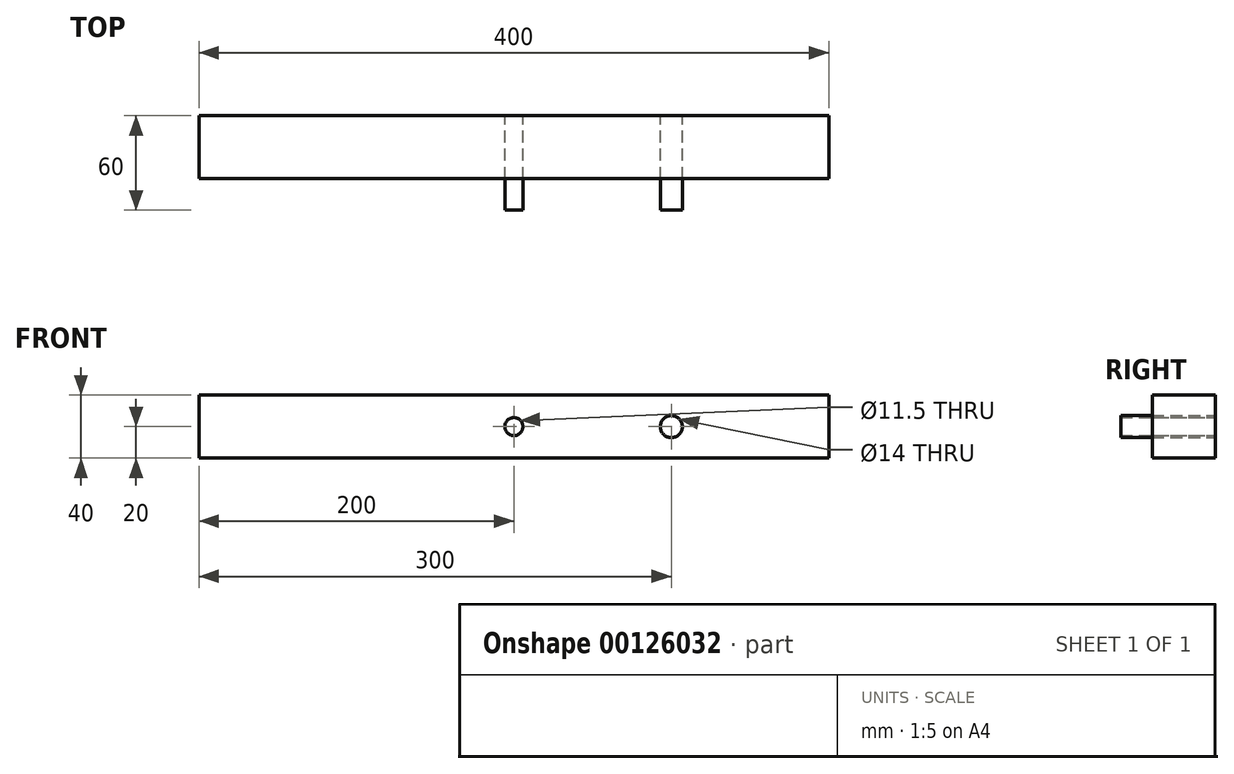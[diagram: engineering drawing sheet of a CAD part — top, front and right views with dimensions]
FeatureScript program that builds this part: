
annotation { "Feature Type Name" : "Feature", "Feature Type Description" : "" }
export const myFeature = defineFeature(function(context is Context, id is Id, definition is map)
    precondition{}
    {
        {
            var Q0;
            Q0=qCreatedBy(makeId("Front.planeOp"),FACE);
            var sketch = newSketch(context, id + "F0", { "sketchPlane" : qUnion([Q0])});
            skLineSegment(sketch, "E0.bottom", {"start": v(200, 20) * mm, "end": v(-200, 20) * mm});
            skLineSegment(sketch, "E0.top", {"start": v(200, -20) * mm, "end": v(-200, -20) * mm});
            skLineSegment(sketch, "E0.left", {"start": v(200, 20) * mm, "end": v(200, -20) * mm});
            skLineSegment(sketch, "E0.right", {"start": v(-200, 20) * mm, "end": v(-200, -20) * mm});
            skPoint(sketch, "E0.middle", {"position": v(0, 0) * mm});
            skCircle(sketch, "E1", {"center": v(0, 0) * mm, "radius": 5.75 * mm});
            skCircle(sketch, "E2", {"center": v(100, 0) * mm, "radius": 7 * mm});
            skSolve(sketch);
        }
        {
            var Q0;
            Q0=makeQuery(id+"F0.imprint","IMPRINT",FACE,{"disambiguationData":[TD([[makeQuery(id+"F0.imprint","IMPRINT",EDGE,{"derivedFrom":sQuery(id+"F0.wireOp",EDGE,"E1")}),1.0]])]});
            var Q1;
            Q1=makeQuery(id+"F0.imprint","IMPRINT",FACE,{"disambiguationData":[TD([[makeQuery(id+"F0.imprint","IMPRINT",EDGE,{"derivedFrom":sQuery(id+"F0.wireOp",EDGE,"E2")}),1.0]])]});
            extrude(context, id + "F1", {"entities" : qUnion([Q0, Q1]), "depth" : 60 * mm});
        }
        {
            var Q0;
            Q0 = qSketchRegion(id + "F0", true);
            extrude(context, id + "F2", {"entities" : qUnion([Q0]), "depth" : 40 * mm});
        }
    });
